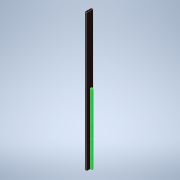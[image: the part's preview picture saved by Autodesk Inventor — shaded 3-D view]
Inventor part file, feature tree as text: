
AUTODESK INVENTOR PART (.ipt)
format: ipt  version: 2022 (Build 260153000, 153)  size: 120,320 bytes
history: native  units: mm
features: extrude x2, sketch x2, fillet x1
ambient origin geometry x8: Origin, YZ Plane, XZ Plane, XY Plane, X Axis, Y Axis, Z Axis, Center Point
bodies: Solid1 (feature_tree)
feature tree (5):
  extrude  "Extrusion1"  Depth=2.0mm TaperAngle=0.0deg
  extrude  "Extrusion2"  Depth=1.0mm
  fillet  "Fillet1"  [1 undecoded]
  sketch  "Sketch1"  dims[d0=150.0mm d1=2.0mm d2=0.0mm]
  sketch  "Sketch2"  dims[d3=2.0mm d4=0.0mm d5=1.0mm]
note: 1 required parameter value undecoded (feature->parameter linkage not recoverable at this tier; creation-order binding heuristic only, values carry confidence <= 0.55)
